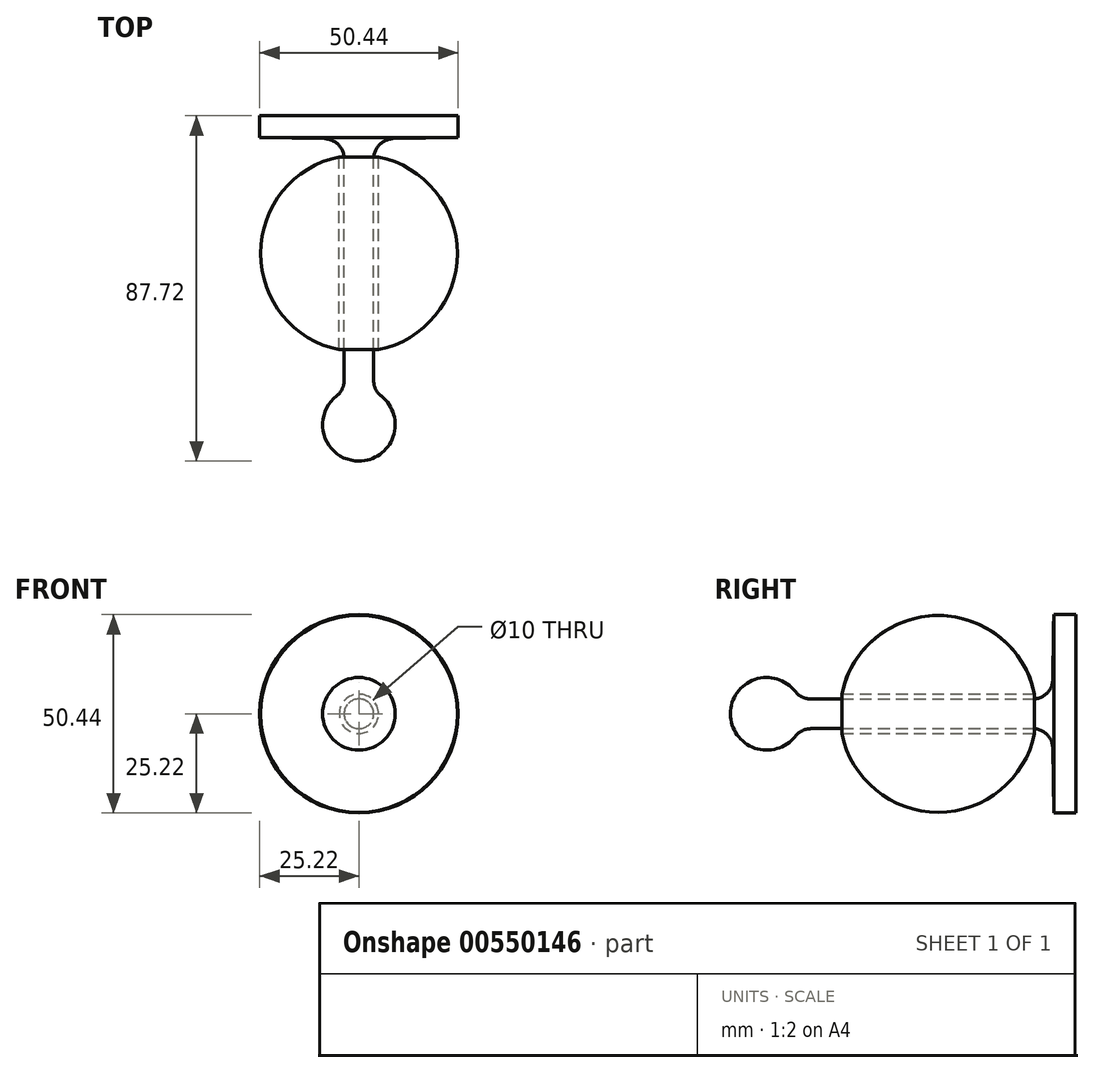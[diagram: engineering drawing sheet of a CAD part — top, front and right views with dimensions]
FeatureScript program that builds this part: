
annotation { "Feature Type Name" : "Feature", "Feature Type Description" : "" }
export const myFeature = defineFeature(function(context is Context, id is Id, definition is map)
    precondition{}
    {
        {
            var Q0;
            Q0=qCreatedBy(makeId("Top.planeOp"),FACE);
            var sketch = newSketch(context, id + "F0", { "sketchPlane" : qUnion([Q0])});
            skArc(sketch, "E0", {"start": v(-5, 24.5) * mm, "mid": v(-25, 0) * mm, "end": v(-5, -24.5) * mm});
            skLineSegment(sketch, "E1", {"start": v(0, 25) * mm, "end": v(0, -25) * mm});
            skLineSegment(sketch, "E2.left", {"start": v(5, -24.5) * mm, "end": v(5, 24.5) * mm});
            skLineSegment(sketch, "E2.right", {"start": v(-5, -24.5) * mm, "end": v(-5, 24.5) * mm});
            skArc(sketch, "E3.trimOffspring", {"start": v(5, -24.5) * mm, "mid": v(25, 0) * mm, "end": v(5, 24.5) * mm});
            skPoint(sketch, "E4.orphan", {"position": v(5, 29.04) * mm});
            skPoint(sketch, "E5.orphan", {"position": v(-5, 29.04) * mm});
            skPoint(sketch, "E2.bottom.start.orphan", {"position": v(5, -29.04) * mm});
            skPoint(sketch, "E6.orphan", {"position": v(-5, -29.04) * mm});
            skLineSegment(sketch, "E7", {"start": v(0, 25) * mm, "end": v(0, 34.94) * mm});
            skLineSegment(sketch, "E8", {"start": v(0, 34.94) * mm, "end": v(25.22, 34.94) * mm});
            skLineSegment(sketch, "E9", {"start": v(25.22, 34.94) * mm, "end": v(25.22, 29.36) * mm});
            skLineSegment(sketch, "E10", {"start": v(25.22, 29.36) * mm, "end": v(3.77, 29.04) * mm});
            skLineSegment(sketch, "E11", {"start": v(3.77, 29.04) * mm, "end": v(3.77, -35.13) * mm});
            skLineSegment(sketch, "E12", {"start": v(0, -43.55) * mm, "end": v(0, -25) * mm});
            skArc(sketch, "E13", {"start": v(0, -52.78) * mm, "mid": v(9.02, -45.48) * mm, "end": v(3.77, -35.13) * mm});
            skLineSegment(sketch, "E14", {"start": v(0, -43.55) * mm, "end": v(0, -52.78) * mm});
            skSolve(sketch);
        }
        {
            var Q0;
            Q0=makeQuery(id+"F0.imprint","IMPRINT",FACE,{"disambiguationData":[TD([[makeQuery(id+"F0.imprint","IMPRINT",EDGE,{"derivedFrom":sQuery(id+"F0.wireOp",EDGE,"E2.left")}),-1.0]])]});
            var Q1;
            Q1=sQuery(id+"F0.wireOp",EDGE,"E1");
            revolve(context, id + "F1", {"entities" : qUnion([Q0]), "axis" : qUnion([Q1]), "revolveType" : RevolveType.FULL});
        }
        {
            var Q0;
            Q0=makeQuery(id+"F0.imprint","IMPRINT",FACE,{"disambiguationData":[TD([[makeQuery(id+"F0.imprint","IMPRINT",EDGE,{"derivedFrom":sQuery(id+"F0.wireOp",EDGE,"E1")}),1.0]])]});
            var Q1;
            Q1=sQuery(id+"F0.wireOp",EDGE,"E1");
            revolve(context, id + "F2", {"entities" : qUnion([Q0]), "axis" : qUnion([Q1]), "revolveType" : RevolveType.FULL});
        }
        {
            var Q0;
            Q0=makeQuery(id+"F2.opRevolve","SWEPT_EDGE",EDGE,{"disambiguationData":[OSD([sQuery(id+"F0.wireOp",EDGE,"E11"),sQuery(id+"F0.wireOp",EDGE,"ZmCsV7Aw-4625-WoId-fea7-rP3SYHAgtjdh")])]});
            var Q1;
            Q1=makeQuery(id+"F2.opRevolve","SWEPT_EDGE",EDGE,{"disambiguationData":[OSD([sQuery(id+"F0.wireOp",EDGE,"E10"),sQuery(id+"F0.wireOp",EDGE,"E11")])]});
            fillet(context, id + "F3", {"entities" : qUnion([Q0, Q1]), "radius" : 5 * mm, "tangentPropagation" : true, "allowEdgeOverflow" : false});
        }
    });
